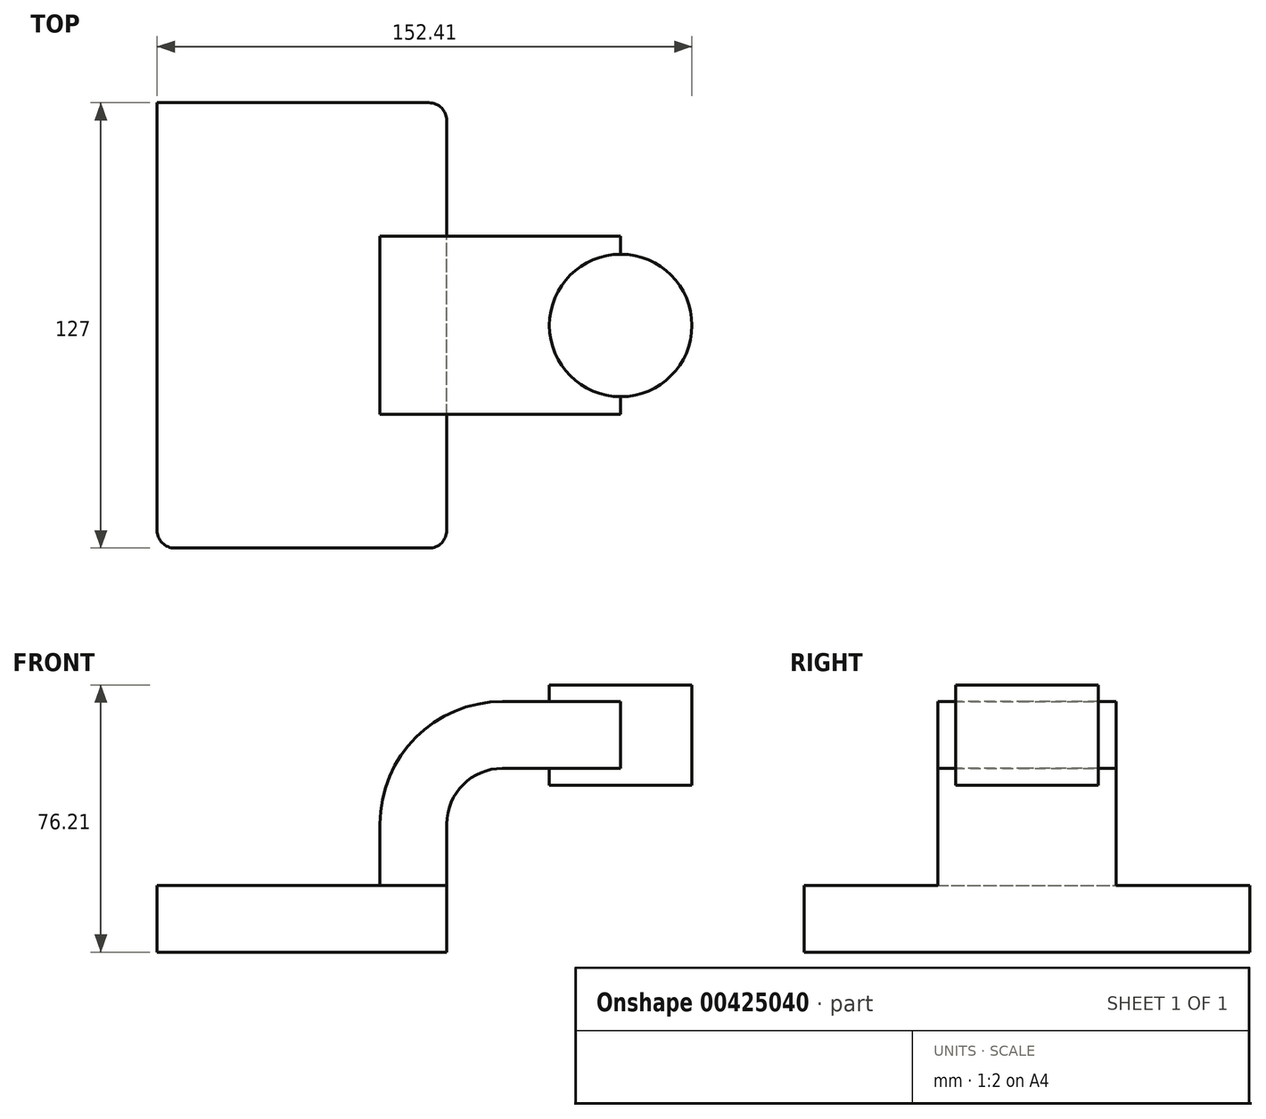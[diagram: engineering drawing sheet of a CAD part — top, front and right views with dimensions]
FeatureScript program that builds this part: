
annotation { "Feature Type Name" : "Feature", "Feature Type Description" : "" }
export const myFeature = defineFeature(function(context is Context, id is Id, definition is map)
    precondition{}
    {
        {
            var Q0;
            Q0=qCreatedBy(makeId("Front.planeOp"),FACE);
            var sketch = newSketch(context, id + "F0", { "sketchPlane" : qUnion([Q0])});
            skLineSegment(sketch, "E0.bottom", {"start": v(-41.28, -9.53) * mm, "end": v(41.28, -9.53) * mm});
            skLineSegment(sketch, "E0.top", {"start": v(-41.28, 9.53) * mm, "end": v(41.28, 9.53) * mm});
            skLineSegment(sketch, "E0.left", {"start": v(-41.28, -9.53) * mm, "end": v(-41.28, 9.53) * mm});
            skLineSegment(sketch, "E0.right", {"start": v(41.28, -9.53) * mm, "end": v(41.28, 9.53) * mm});
            skPoint(sketch, "E0.middle", {"position": v(0, 0) * mm});
            skLineSegment(sketch, "E1.bottom", {"start": v(60.32, 38.1) * mm, "end": v(111.12, 38.1) * mm});
            skLineSegment(sketch, "E1.top", {"start": v(60.32, 66.67) * mm, "end": v(111.12, 66.67) * mm});
            skLineSegment(sketch, "E1.left", {"start": v(60.32, 38.1) * mm, "end": v(60.32, 66.67) * mm});
            skLineSegment(sketch, "E1.right", {"start": v(111.12, 38.1) * mm, "end": v(111.12, 66.67) * mm});
            skPoint(sketch, "E1.middle", {"position": v(85.72, 52.39) * mm});
            skLineSegment(sketch, "E2", {"start": v(41.28, 9.53) * mm, "end": v(41.28, 27) * mm});
            skArc(sketch, "E3", {"start": v(41.27, 27) * mm, "mid": v(45.92, 38.23) * mm, "end": v(57.15, 42.88) * mm});
            skLineSegment(sketch, "E4", {"start": v(57.15, 42.88) * mm, "end": v(90.82, 42.88) * mm});
            skLineSegment(sketch, "E5.0", {"start": v(57.15, 61.93) * mm, "end": v(90.82, 61.93) * mm});
            skArc(sketch, "E5.1", {"start": v(22.22, 27) * mm, "mid": v(32.45, 51.7) * mm, "end": v(57.15, 61.93) * mm});
            skLineSegment(sketch, "E5.2", {"start": v(22.22, 9.53) * mm, "end": v(22.22, 27) * mm});
            skLineSegment(sketch, "E6", {"start": v(90.82, 38.1) * mm, "end": v(90.82, 66.67) * mm});
            skFitSpline(sketch, "E7", {"points": [v(-41.28, 9.53) * mm, v(57.15, 61.93) * mm], "startDerivative": vector(0.7, 107.89) * mm, "endDerivative": vector(171.45, 0.1) * mm});
            skSolve(sketch);
        }
        {
            var Q0;
            Q0=makeQuery(id+"F0.imprint","IMPRINT",FACE,{"disambiguationData":[TD([[makeQuery(id+"F0.imprint","IMPRINT",EDGE,{"derivedFrom":sQuery(id+"F0.wireOp",EDGE,"E0.bottom")}),1.0]])]});
            extrude(context, id + "F1", {"entities" : qUnion([Q0]), "endBound" : BoundingType.SYMMETRIC, "depth" : 127 * mm});
        }
        {
            var Q0;
            {var subQ1=sQuery(id+"F0.wireOp",EDGE,"E2");Q0=makeQuery(id+"F0.imprint","IMPRINT",FACE,{"disambiguationData":[TD([[makeQuery(id+"F0.imprint","IMPRINT",EDGE,{"derivedFrom":subQ1}),1.0]])]});}
            var Q1;
            {var subQ0=sQuery(id+"F0.wireOp",EDGE,"E4");var subQ1=sQuery(id+"F0.wireOp",EDGE,"E1.left");var subQ2=makeQuery(id+"F0.imprint","INTERSECT",VERTEX,{"derivedFrom":[subQ1,subQ0]});Q1=makeQuery(id+"F0.imprint","IMPRINT",FACE,{"disambiguationData":[TD([[makeQuery(id+"F0.imprint","IMPRINT",EDGE,{"disambiguationData":[TD([[subQ2,-1.0]])],"derivedFrom":subQ1}),-1.0]])]});}
            extrude(context, id + "F2", {"entities" : qUnion([Q0, Q1]), "operationType" : NewBodyOperationType.ADD, "endBound" : BoundingType.SYMMETRIC, "depth" : 50.8 * mm});
        }
        {
            var Q0;
            Q0=makeQuery(id+"F0.imprint","IMPRINT",FACE,{"disambiguationData":[TD([[makeQuery(id+"F0.imprint","IMPRINT",EDGE,{"derivedFrom":sQuery(id+"F0.wireOp",EDGE,"E5.1")}),1.0]])]});
            extrude(context, id + "F3", {"entities" : qUnion([Q0]), "operationType" : NewBodyOperationType.ADD, "endBound" : BoundingType.SYMMETRIC, "depth" : 15.88 * mm});
        }
        {
            var Q0;
            {var subQ0=sQuery(id+"F0.wireOp",EDGE,"E1.right");Q0=makeQuery(id+"F0.imprint","IMPRINT",FACE,{"disambiguationData":[TD([[makeQuery(id+"F0.imprint","IMPRINT",EDGE,{"derivedFrom":subQ0}),1.0]])]});}
            var Q1;
            Q1=sQuery(id+"F0.wireOp",EDGE,"E6");
            revolve(context, id + "F4", {"operationType" : NewBodyOperationType.ADD, "entities" : qUnion([Q0]), "axis" : qUnion([Q1]), "revolveType" : RevolveType.FULL});
        }
        {
            var Q0;
            Q0=makeQuery(id+"F1.opExtrude","CAP_EDGE",EDGE,{"disambiguationData":[OSD([sQuery(id+"F0.wireOp",EDGE,"E0.right")])],"isStart":false});
            var Q1;
            Q1=makeQuery(id+"F1.opExtrude","CAP_EDGE",EDGE,{"disambiguationData":[OSD([sQuery(id+"F0.wireOp",EDGE,"E0.right")])],"isStart":true});
            var Q2;
            Q2=makeQuery(id+"F1.opExtrude","CAP_EDGE",EDGE,{"disambiguationData":[OSD([sQuery(id+"F0.wireOp",EDGE,"E0.left")])],"isStart":false});
            fillet(context, id + "F5", {"entities" : qUnion([Q0, Q1, Q2]), "radius" : 5.08 * mm, "tangentPropagation" : true, "allowEdgeOverflow" : false});
        }
    });
